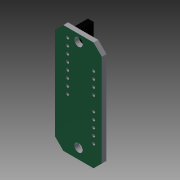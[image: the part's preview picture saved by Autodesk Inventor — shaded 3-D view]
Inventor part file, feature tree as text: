
AUTODESK INVENTOR PART (.ipt)
format: ipt  version: 2015 (Build 190159000, 159)  size: 186,368 bytes
history: native  units: mm
features: extrude x7, sketch x2, fillet x1
ambient origin geometry x8: Origin, YZ Plane, XZ Plane, XY Plane, X Axis, Y Axis, Z Axis, Center Point
bodies: Solid1 (feature_tree)
feature tree (10):
  sketch  "Sketch1"  dims[d0=17.0mm d1=39.65mm]
  extrude  "Extrusion2"  Depth=39.65mm
  extrude  "Extrusion3"  Depth=10.0mm
  extrude  "Extrusion4"  Depth=10.0mm
  extrude  "Extrusion5"  Depth=10.0mm
  fillet  "Fillet1"  Radius=3.0mm
  sketch  "Sketch2"  dims[d2=3.0mm d3=3.0mm d4=3.0mm d5=3.0mm d6=3.0mm d7=3.0mm d8=3.0mm d9=3.0mm d10=1.0mm d11=1.0mm d12=1.0mm d13=1.0mm d14=1.0mm d15=1.0mm d16=1.0mm d17=2.54mm d18=2.54mm d19=2.54mm d20=2.54mm d21=2.54mm d23=3.0mm d24=1.0mm d25=1.0mm d26=1.0mm d27=1.0mm d28=2.54mm d29=2.54mm d30=2.54mm d31=1.0mm d32=1.0mm d33=1.0mm d34=1.0mm d35=2.54mm d36=2.54mm d37=2.54mm d39=2.54mm d42=8.4mm d43=0.0mm d44=5.0mm d45=0.0mm d46=1.7mm d47=0.0mm d48=1.7mm d49=0.0mm d50=1.0mm d51=3.0mm d52=3.0mm d53=2.6mm d54=3.72mm d55=10.0mm d56=0.0mm d57=10.0mm d58=0.0mm d59=33.33mm d60=1.0mm d61=2.54mm d62=2.54mm d63=1.330315mm d64=1.330315mm d65=10.0mm d66=0.0mm]
  extrude  "Extrusion6"  Depth=10.0mm
  extrude  "Extrusion7"  Depth=10.0mm
  extrude  "Extrusion8"  Depth=10.0mm
